# Revit family: 0047584 Feilo Sylvania Lighting Fixture SYLPROOF TUBULAR LED 2X1200 EB NW
name_source: partatom
category: Lighting Fixtures
revit_build: Autodesk Revit 2017 (Build: 20190507_1515(x64)
units: mm (PartAtom-declared; Revit-internal decimal feet)

## family parameters
Cut with Voids When Loaded = No
Host = Face
Light Source = Yes
OmniClass Number = 23.80.70.00
OmniClass Title = Lighting
Part Type = Normal
Room Calculation Point = No
Round Connector Dimension = Use Diameter
Shared = No

## types (1)
- 0047584 SYLPROOF TUBULAR LED 2X1200 EB NW
    AccessoryMaterial = <By Category>
    Apparent Load = 39 VA
    Assembly Code = D5020200
    AssetType = Fixed
    BodyMaterial = Body-Sylvania-SylproofTubular-Aluminium
    BracketDistance_FEILO = 1100 mm
    BracketWidth_FEILO = 25 mm  [stored 0.082021 ft]
    ClassificationName = Uniclass2015
    ClassificationValue = EF_70_80
    Color Filter = 16777215
    Cost = 0 $
    Default Elevation = 1219 mm
    Description = Aesthetically attractive and highly efficient LED tubular luminaire, opaque acrylic diffuser, stainless steel end caps and mounting brackets, rapid connector, as Sylvania Sylproof Tubular LED
    DiffuserMaterial = Diffuser-Sylvania-SylproofTubular-Opal
    Dimming Lamp Color Temperature Shift = <None>
    DimmingControlOptions = Non dimmable
    DocumentationLiterature = http://www.sylvania-lighting.com
    DurationUnit = hours
    ElectricShockClassification = Class I
    Emit Shape Visible in Rendering = No
    Emit from Rectangle Length = 90 mm  [stored 0.295276 ft]
    Emit from Rectangle Width = 1222 mm  [stored 4.00919 ft]
    ExpectedLife = 50000
    Height_FEILO = 115 mm
    IfcExportAs = IfcLightFixtureType
    IfcExportType = IfcLightFixtureType
    ImpactProtectionIndex = IK06
    IngressProtection = IP66
    InputNominalFrequency = 50/60 Hz
    InputVoltage = 220-240V~
    Keynote = 16500
    Lamp = LED
    LampColourRenderingIndex = 0
    LampColourTemperature = 4000 K
    LampNominalLuminous = 4264 lm
    LampsType = LED
    LightOutputRatio = 100
    LuminousEfficacy = 109.33 lm/W
    Manufacturer = Feilo Sylvania
    ManufacturerName = Feilo Sylvania
    Material = acrylic/pmma tube housing, acrylic/pmma diffuser
    Model = SYLPROOF TUBULAR LED 2X1200 EB NW
    ModelNumber = 0047584
    ModelReference = SYLPROOF TUBULAR LED 2X1200 EB NW
    MountingHeight_FEILO = 64 mm
    Name = SYLPROOF TUBULAR LED 2X1200 EB NW
    NominalDepth = 112 mm
    NominalHeight = 112 mm
    NominalLength = 1300 mm
    Photometric Web File = 0047584.ies
    PowerConsumption = 39 W
    PowerFactor = 0
    ReflectorMaterial = Reflector-Sylvania-SylproofTubular-Illumination
    Tilt Angle = -90.00°
    TubeDiameterInside_FEILO = 96 mm  [stored 0.314961 ft]
    TubeDiameterOutside_FEILO = 100 mm  [stored 0.328084 ft]
    TubeLength_FEILO = 1242 mm  [stored 4.0748 ft]
    Type Image = <None>
    TypeName = SYLPROOF TUBULAR LED 2X1200 EB NW
    URL = http://www.sylvania-lighting.com
    Voltage = 230 V
    Weight = 2.6 kg

note: [stored X ft] marks values corroborated as IEEE doubles in the binary element streams (Revit-internal decimal feet)

## geometry (parser evidence)
native form markers: Sweep x3
no freeform markers — native parametric forms only
